# Revit family: Zumtobel CLEAN II
name_source: partatom
category: Lighting Fixtures
revit_build: Autodesk Revit 2018 (Build: 20170223_1515(x64)
units: mm (PartAtom-declared; Revit-internal decimal feet)

## family parameters
Cut with Voids When Loaded = No
Host = Face
Light Source = Yes
OmniClass Number = 23.80.70.11
OmniClass Title = Luminaries for Internal Lighting
Part Type = Normal
Room Calculation Point = No
Round Connector Dimension = Use Diameter
Shared = No

## types (6) — shared parameters
Assembly Code = D5020200
Body = ZGl_Metal_Aluminium
Color Filter = 16777215
Cover = ZG_PMMA_Self_llumination_Opaque
Dimming Lamp Color Temperature Shift = <None>
Emit Shape Visible in Rendering = Yes
Lamp = LED
Manufacturer = Zumtobel Lighting
Tilt Angle = 90.00°
URL = http://www.zumtobel.com
Voltage = 230 V
zero-valued in all types: Default Elevation

## per-type parameters (varying)
| type | Apparent Load | Description | Emit from Rectangle Length | Emit from Rectangle Width | Height | Length | Model | Offset | Photometric Web File | Recessed | Surface Mount | Top Offset | Width |
| CL2 I 4600-840 M600Q PM O LDO | 40 VA | Surface mount luminaire | 589 mm | 589 mm | 57 mm  [stored 0.187008 ft] | 609 mm | 42186912 | 200 mm  [stored 0.656168 ft] | 42186912_(STD_LEO).IES | No | Yes | 57 mm  [stored 0.187008 ft] | 609 mm |
| CL2 S 4600-940 Q610 SG MP LDO | 34 VA | Surface mount luminaire | 589 mm | 589 mm | 57 mm  [stored 0.187008 ft] | 609 mm | 42186912 | 200 mm  [stored 0.656168 ft] | 42186880_(STD_LEO).IES | No | Yes | 57 mm  [stored 0.187008 ft] | 609 mm |
| CL2 I 4600-840 M600L PM O LDO | 35 VA | Recessed Luminaire | 278 mm | 1178 mm | 105 mm | 1198 mm | 42186884 | 0 mm  [stored 0 ft] | 42186884_(STD_LEO).IES | Yes | No | 0 mm  [stored 0 ft] | 298 mm |
| CL2 S 6600-840 M625Q SG MP LDO | 50 VA | Recessed Luminaire | 603 mm | 603 mm | 100 mm  [stored 0.328084 ft] | 623 mm | 42186891 | 0 mm  [stored 0 ft] | 42186891_(STD_LEO).IES | Yes | No | 0 mm  [stored 0 ft] | 623 mm |
| CL2 S 8000-940 L1250 SG MP LDO | 80 VA | Surface mount luminaire | 329 mm  [stored 1.0794 ft] | 1229 mm  [stored 4.03215 ft] | 57 mm  [stored 0.187008 ft] | 1249 mm  [stored 4.09777 ft] | 42186915 | 200 mm  [stored 0.656168 ft] | 42186915_(STD_LEO).IES | No | Yes | 57 mm  [stored 0.187008 ft] | 349 mm  [stored 1.14501 ft] |
| CL2 S 10000-940 L1550 SG MP LDO | 96 VA | Surface mount luminaire | 329 mm  [stored 1.0794 ft] | 1529 mm | 57 mm  [stored 0.187008 ft] | 1549 mm | 42186916 | 200 mm  [stored 0.656168 ft] | 42186916_(STD_LEO).IES | No | Yes | 57 mm  [stored 0.187008 ft] | 349 mm  [stored 1.14501 ft] |

note: [stored X ft] marks values corroborated as IEEE doubles in the binary element streams (Revit-internal decimal feet)

## geometry (parser evidence)
native form markers: Sweep x3
no freeform markers — native parametric forms only
